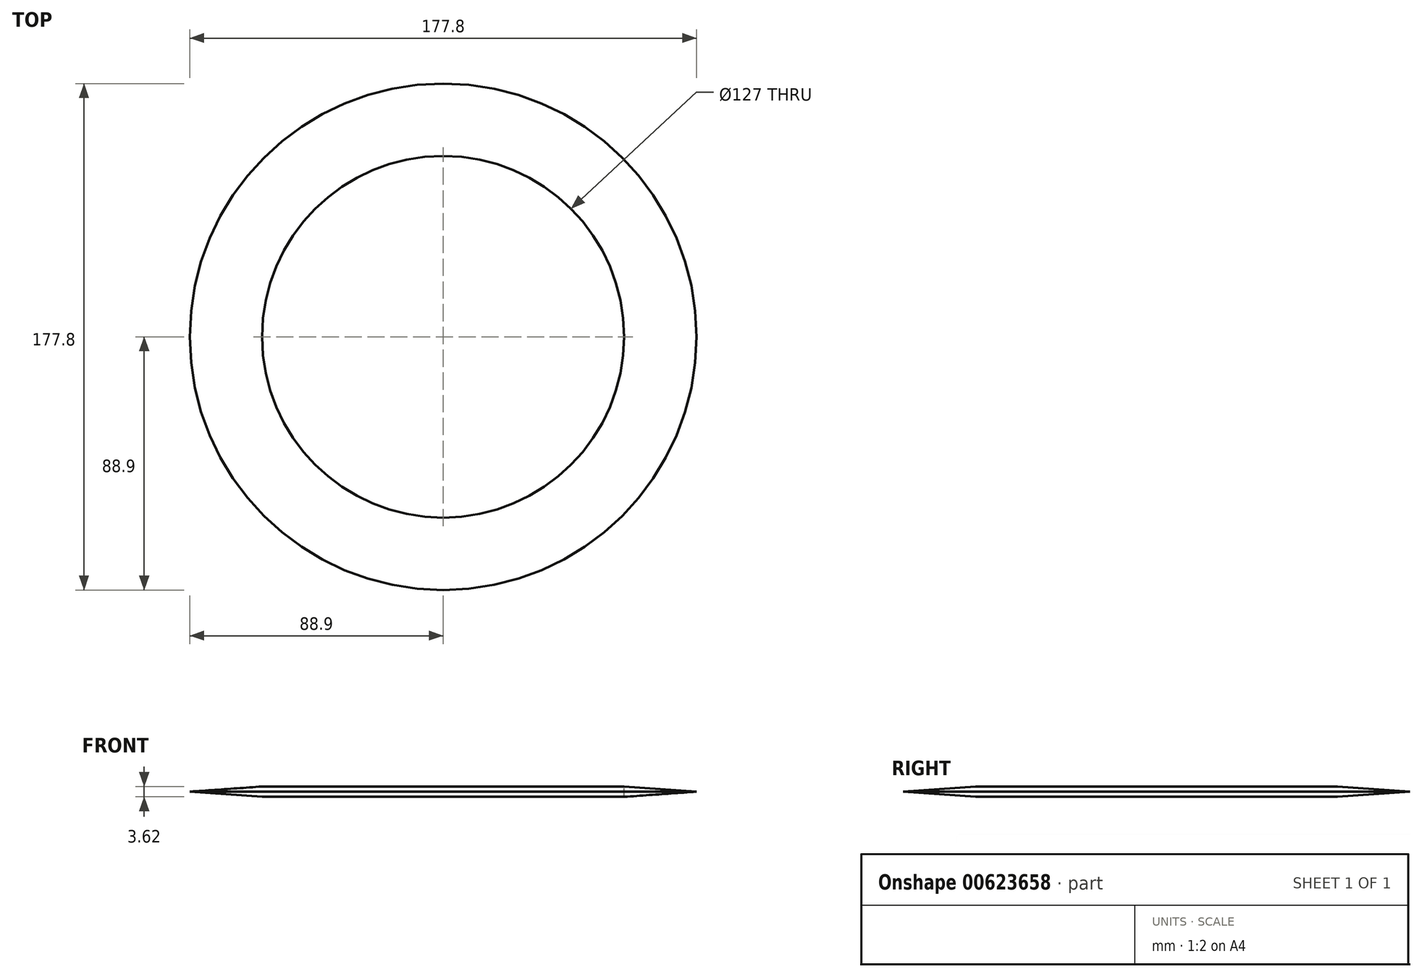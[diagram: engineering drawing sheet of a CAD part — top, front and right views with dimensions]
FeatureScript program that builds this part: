
annotation { "Feature Type Name" : "Feature", "Feature Type Description" : "" }
export const myFeature = defineFeature(function(context is Context, id is Id, definition is map)
    precondition{}
    {
        {
            var Q0;
            Q0=qCreatedBy(makeId("Top.planeOp"),FACE);
            var sketch = newSketch(context, id + "F0", { "sketchPlane" : qUnion([Q0])});
            skCircle(sketch, "E0", {"center": v(0, 0) * mm, "radius": 88.9 * mm});
            skCircle(sketch, "E1", {"center": v(0, 0) * mm, "radius": 63.5 * mm});
            skSolve(sketch);
        }
        {
            var Q0;
            Q0=qCreatedBy(makeId("Front.planeOp"),FACE);
            var sketch = newSketch(context, id + "F1", { "sketchPlane" : qUnion([Q0])});
            skLineSegment(sketch, "E2", {"start": v(-88.9, 0) * mm, "end": v(0, 6.35) * mm});
            skLineSegment(sketch, "E3.MirrorCS", {"start": v(-88.9, 0) * mm, "end": v(0, -6.35) * mm});
            skLineSegment(sketch, "E4", {"start": v(0, -6.35) * mm, "end": v(0, 6.35) * mm, "construction": true});
            skLineSegment(sketch, "E5.bottom", {"start": v(0, 6.35) * mm, "end": v(-88.9, 6.35) * mm});
            skLineSegment(sketch, "E5.top", {"start": v(0, -6.35) * mm, "end": v(-88.9, -6.35) * mm});
            skLineSegment(sketch, "E5.left", {"start": v(0, 6.35) * mm, "end": v(0, -6.35) * mm});
            skLineSegment(sketch, "E5.right", {"start": v(-88.9, 6.35) * mm, "end": v(-88.9, -6.35) * mm});
            skLineSegment(sketch, "E6", {"start": v(-63.39, 6.35) * mm, "end": v(-63.39, -6.35) * mm, "construction": true});
            skLineSegment(sketch, "E7", {"start": v(-63.39, 1.82) * mm, "end": v(-51.4, 1.82) * mm, "construction": true});
            skLineSegment(sketch, "E8", {"start": v(-63.39, -1.82) * mm, "end": v(-51.28, -1.82) * mm, "construction": true});
            skSolve(sketch);
        }
        {
            var Q0;
            {var subQ0=sQuery(id+"F1.wireOp",EDGE,"E2");Q0=makeQuery(id+"F1.imprint","IMPRINT",FACE,{"disambiguationData":[TD([[makeQuery(id+"F1.imprint","IMPRINT",EDGE,{"derivedFrom":subQ0}),-1.0]])]});}
            var Q1;
            Q1=sQuery(id+"F1.wireOp",EDGE,"E4");
            revolve(context, id + "F2", {"entities" : qUnion([Q0]), "axis" : qUnion([Q1]), "revolveType" : RevolveType.ONE_DIRECTION, "oppositeDirection" : true, "angle" : 360 * degree});
        }
        {
            var Q0;
            Q0=makeQuery(id+"F0.imprint","IMPRINT",FACE,{"disambiguationData":[TD([[makeQuery(id+"F0.imprint","IMPRINT",EDGE,{"derivedFrom":sQuery(id+"F0.wireOp",EDGE,"E1")}),1.0]])]});
            extrude(context, id + "F3", {"entities" : qUnion([Q0]), "operationType" : NewBodyOperationType.REMOVE, "oppositeDirection" : true, "depth" : 33.02 * mm, "offsetDistance" : 25.4 * mm, "hasSecondDirection" : true, "secondDirectionOppositeDirection" : false, "secondDirectionDepth" : 49.02 * mm});
        }
    });
